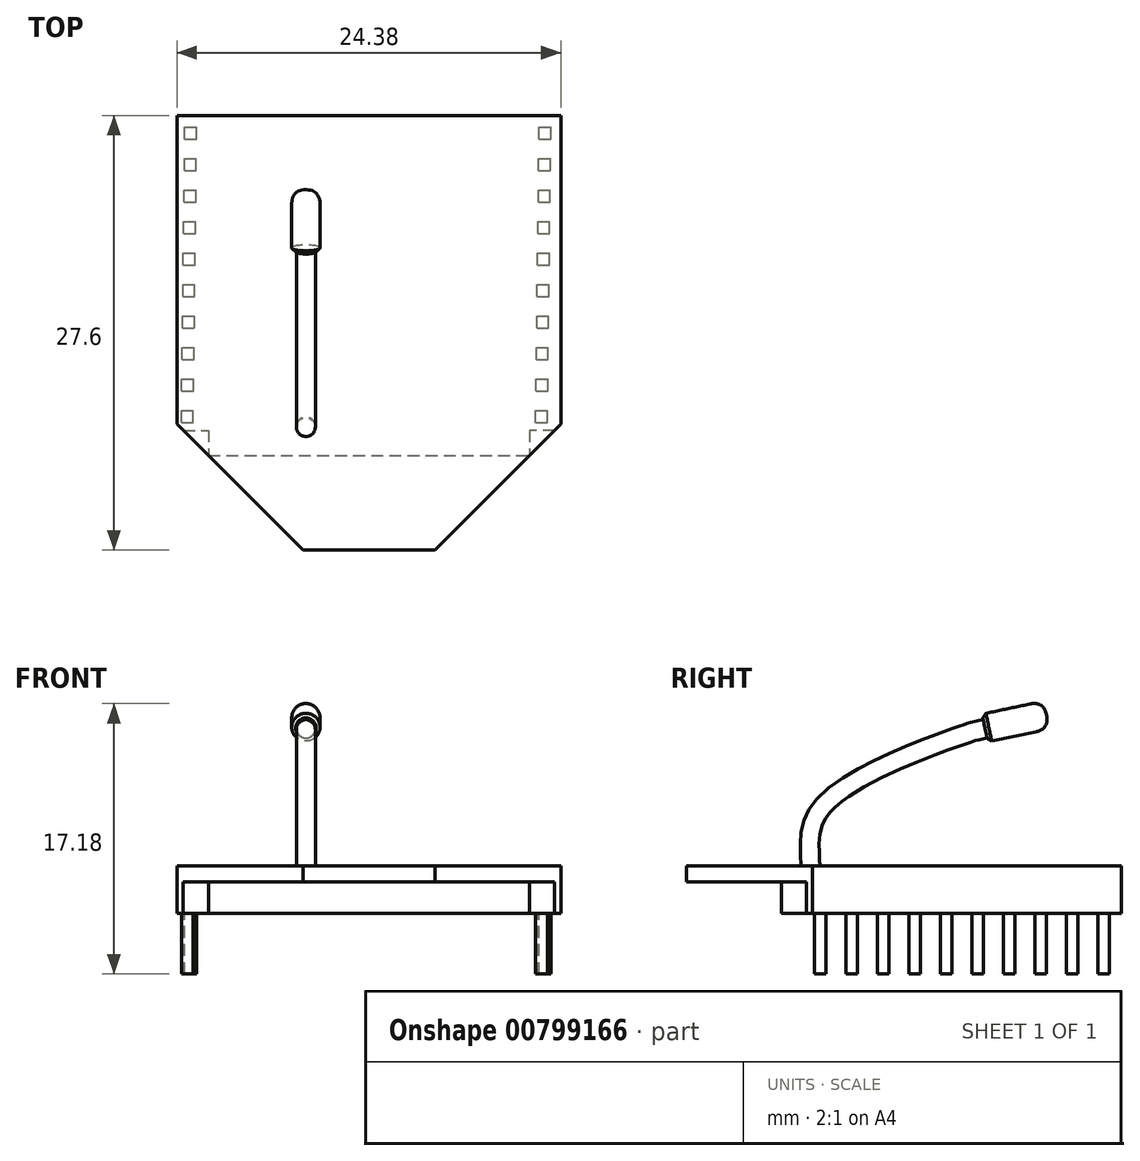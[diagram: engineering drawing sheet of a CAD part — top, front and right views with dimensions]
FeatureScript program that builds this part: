
annotation { "Feature Type Name" : "Feature", "Feature Type Description" : "" }
export const myFeature = defineFeature(function(context is Context, id is Id, definition is map)
    precondition{}
    {
        {
            var Q0;
            Q0=qCreatedBy(makeId("Top.planeOp"),FACE);
            var sketch = newSketch(context, id + "F0", { "sketchPlane" : qUnion([Q0])});
            skLineSegment(sketch, "E0.bottom", {"start": v(-12.19, 13.8) * mm, "end": v(12.2, 13.8) * mm});
            skLineSegment(sketch, "E0.top", {"start": v(-12.2, -13.8) * mm, "end": v(12.2, -13.8) * mm});
            skLineSegment(sketch, "E0.left", {"start": v(-12.19, 13.8) * mm, "end": v(-12.2, -13.8) * mm});
            skLineSegment(sketch, "E0.right", {"start": v(12.2, 13.8) * mm, "end": v(12.19, -13.8) * mm});
            skPoint(sketch, "E0.middle", {"position": v(0, 0) * mm});
            skSolve(sketch);
        }
        {
            var Q0;
            Q0 = qSketchRegion(id + "F0", true);
            extrude(context, id + "F1", {"entities" : qUnion([Q0]), "oppositeDirection" : true, "depth" : 1 * mm, "offsetDistance" : 25 * mm});
        }
        {
            var Q0;
            Q0=makeQuery(id+"F1.opExtrude","CAP_FACE",FACE,{"disambiguationData":[OSD([sQuery(id+"F0.wireOp",EDGE,"E0.bottom"),sQuery(id+"F0.wireOp",EDGE,"E0.top"),sQuery(id+"F0.wireOp",EDGE,"E0.left"),sQuery(id+"F0.wireOp",EDGE,"E0.right")])],"isStart":false});
            var sketch = newSketch(context, id + "F2", { "sketchPlane" : qUnion([Q0])});
            skLineSegment(sketch, "E1.bottom", {"start": v(-12.19, -13.8) * mm, "end": v(-10.19, -13.8) * mm});
            skLineSegment(sketch, "E1.top", {"start": v(-12.2, 6.2) * mm, "end": v(-10.2, 6.2) * mm});
            skLineSegment(sketch, "E1.left", {"start": v(-12.19, -13.8) * mm, "end": v(-12.19, 6.2) * mm});
            skLineSegment(sketch, "E1.right", {"start": v(-10.19, -13.8) * mm, "end": v(-10.2, 6.2) * mm});
            skLineSegment(sketch, "E2.bottom", {"start": v(12.2, -13.8) * mm, "end": v(10.2, -13.8) * mm});
            skLineSegment(sketch, "E2.top", {"start": v(12.2, 6.2) * mm, "end": v(10.2, 6.2) * mm});
            skLineSegment(sketch, "E2.left", {"start": v(12.2, -13.8) * mm, "end": v(12.2, 6.2) * mm});
            skLineSegment(sketch, "E2.right", {"start": v(10.2, -13.8) * mm, "end": v(10.2, 6.2) * mm});
            skSolve(sketch);
        }
        {
            var Q0;
            Q0=makeQuery(id+"F2.imprint","IMPRINT",FACE,{"disambiguationData":[TD([[makeQuery(id+"F2.imprint","IMPRINT",EDGE,{"derivedFrom":sQuery(id+"F2.wireOp",EDGE,"E1.bottom")}),1.0]])]});
            var Q1;
            Q1=makeQuery(id+"F2.imprint","IMPRINT",FACE,{"disambiguationData":[TD([[makeQuery(id+"F2.imprint","IMPRINT",EDGE,{"derivedFrom":sQuery(id+"F2.wireOp",EDGE,"E2.bottom")}),1.0]])]});
            extrude(context, id + "F3", {"entities" : qUnion([Q0, Q1]), "operationType" : NewBodyOperationType.ADD, "depth" : 2 * mm, "offsetDistance" : 25 * mm});
        }
        {
            var Q0;
            Q0=makeQuery(id+"F3.opExtrude","CAP_FACE",FACE,{"disambiguationData":[OSD([sQuery(id+"F2.wireOp",EDGE,"E1.bottom"),sQuery(id+"F2.wireOp",EDGE,"E1.top"),sQuery(id+"F2.wireOp",EDGE,"E1.left"),sQuery(id+"F2.wireOp",EDGE,"E1.right")])],"isStart":false});
            var sketch = newSketch(context, id + "F4", { "sketchPlane" : qUnion([Q0])});
            skLineSegment(sketch, "E3.bottom", {"start": v(-11.69, -12.3) * mm, "end": v(-10.94, -12.3) * mm});
            skLineSegment(sketch, "E3.top", {"start": v(-11.69, -13.05) * mm, "end": v(-10.94, -13.05) * mm});
            skLineSegment(sketch, "E3.left", {"start": v(-11.69, -12.3) * mm, "end": v(-11.69, -13.05) * mm});
            skLineSegment(sketch, "E3.right", {"start": v(-10.94, -12.3) * mm, "end": v(-10.94, -13.05) * mm});
            skLineSegment(sketch, "E4.0.1.0", {"start": v(-11.71, -10.3) * mm, "end": v(-10.96, -10.3) * mm});
            skLineSegment(sketch, "E4.0.1.1", {"start": v(-10.96, -10.3) * mm, "end": v(-10.96, -11.06) * mm});
            skLineSegment(sketch, "E4.0.1.2", {"start": v(-11.71, -10.3) * mm, "end": v(-11.71, -11.06) * mm});
            skLineSegment(sketch, "E4.0.1.3", {"start": v(-11.71, -11.06) * mm, "end": v(-10.96, -11.06) * mm});
            skLineSegment(sketch, "E4.0.2.0", {"start": v(-11.74, -8.3) * mm, "end": v(-10.99, -8.3) * mm});
            skLineSegment(sketch, "E4.0.2.1", {"start": v(-10.99, -8.3) * mm, "end": v(-10.99, -9.06) * mm});
            skLineSegment(sketch, "E4.0.2.2", {"start": v(-11.74, -8.3) * mm, "end": v(-11.74, -9.06) * mm});
            skLineSegment(sketch, "E4.0.2.3", {"start": v(-11.74, -9.06) * mm, "end": v(-10.99, -9.06) * mm});
            skLineSegment(sketch, "E4.0.3.0", {"start": v(-11.76, -6.3) * mm, "end": v(-11.01, -6.3) * mm});
            skLineSegment(sketch, "E4.0.3.1", {"start": v(-11.01, -6.3) * mm, "end": v(-11.01, -7.06) * mm});
            skLineSegment(sketch, "E4.0.3.2", {"start": v(-11.76, -6.3) * mm, "end": v(-11.76, -7.06) * mm});
            skLineSegment(sketch, "E4.0.3.3", {"start": v(-11.76, -7.06) * mm, "end": v(-11.01, -7.06) * mm});
            skLineSegment(sketch, "E4.0.4.0", {"start": v(-11.79, -4.3) * mm, "end": v(-11.04, -4.3) * mm});
            skLineSegment(sketch, "E4.0.4.1", {"start": v(-11.04, -4.3) * mm, "end": v(-11.04, -5.06) * mm});
            skLineSegment(sketch, "E4.0.4.2", {"start": v(-11.79, -4.3) * mm, "end": v(-11.79, -5.06) * mm});
            skLineSegment(sketch, "E4.0.4.3", {"start": v(-11.79, -5.06) * mm, "end": v(-11.04, -5.06) * mm});
            skLineSegment(sketch, "E4.0.5.0", {"start": v(-11.81, -2.3) * mm, "end": v(-11.06, -2.3) * mm});
            skLineSegment(sketch, "E4.0.5.1", {"start": v(-11.06, -2.3) * mm, "end": v(-11.06, -3.06) * mm});
            skLineSegment(sketch, "E4.0.5.2", {"start": v(-11.81, -2.3) * mm, "end": v(-11.81, -3.06) * mm});
            skLineSegment(sketch, "E4.0.5.3", {"start": v(-11.81, -3.06) * mm, "end": v(-11.06, -3.06) * mm});
            skLineSegment(sketch, "E4.0.6.0", {"start": v(-11.83, -0.3) * mm, "end": v(-11.08, -0.3) * mm});
            skLineSegment(sketch, "E4.0.6.1", {"start": v(-11.08, -0.3) * mm, "end": v(-11.08, -1.06) * mm});
            skLineSegment(sketch, "E4.0.6.2", {"start": v(-11.83, -0.3) * mm, "end": v(-11.83, -1.06) * mm});
            skLineSegment(sketch, "E4.0.6.3", {"start": v(-11.83, -1.06) * mm, "end": v(-11.08, -1.06) * mm});
            skLineSegment(sketch, "E4.0.7.0", {"start": v(-11.86, 1.7) * mm, "end": v(-11.1, 1.7) * mm});
            skLineSegment(sketch, "E4.0.7.1", {"start": v(-11.1, 1.7) * mm, "end": v(-11.1, 0.94) * mm});
            skLineSegment(sketch, "E4.0.7.2", {"start": v(-11.86, 1.7) * mm, "end": v(-11.86, 0.94) * mm});
            skLineSegment(sketch, "E4.0.7.3", {"start": v(-11.86, 0.94) * mm, "end": v(-11.1, 0.94) * mm});
            skLineSegment(sketch, "E4.0.8.0", {"start": v(-11.88, 3.7) * mm, "end": v(-11.13, 3.7) * mm});
            skLineSegment(sketch, "E4.0.8.1", {"start": v(-11.13, 3.7) * mm, "end": v(-11.13, 2.94) * mm});
            skLineSegment(sketch, "E4.0.8.2", {"start": v(-11.88, 3.7) * mm, "end": v(-11.88, 2.94) * mm});
            skLineSegment(sketch, "E4.0.8.3", {"start": v(-11.88, 2.94) * mm, "end": v(-11.13, 2.94) * mm});
            skLineSegment(sketch, "E4.0.9.0", {"start": v(-11.9, 5.7) * mm, "end": v(-11.16, 5.7) * mm});
            skLineSegment(sketch, "E4.0.9.1", {"start": v(-11.16, 5.7) * mm, "end": v(-11.16, 4.94) * mm});
            skLineSegment(sketch, "E4.0.9.2", {"start": v(-11.9, 5.7) * mm, "end": v(-11.9, 4.94) * mm});
            skLineSegment(sketch, "E4.0.9.3", {"start": v(-11.9, 4.94) * mm, "end": v(-11.16, 4.94) * mm});
            skLineSegment(sketch, "E4.1.0.0", {"start": v(10.81, -12.3) * mm, "end": v(11.56, -12.3) * mm});
            skLineSegment(sketch, "E4.1.0.1", {"start": v(11.56, -12.3) * mm, "end": v(11.56, -13.05) * mm});
            skLineSegment(sketch, "E4.1.0.2", {"start": v(10.81, -12.3) * mm, "end": v(10.81, -13.05) * mm});
            skLineSegment(sketch, "E4.1.0.3", {"start": v(10.81, -13.05) * mm, "end": v(11.56, -13.05) * mm});
            skLineSegment(sketch, "E4.1.1.0", {"start": v(10.79, -10.3) * mm, "end": v(11.54, -10.3) * mm});
            skLineSegment(sketch, "E4.1.1.1", {"start": v(11.54, -10.3) * mm, "end": v(11.54, -11.06) * mm});
            skLineSegment(sketch, "E4.1.1.2", {"start": v(10.79, -10.3) * mm, "end": v(10.79, -11.06) * mm});
            skLineSegment(sketch, "E4.1.1.3", {"start": v(10.79, -11.06) * mm, "end": v(11.54, -11.06) * mm});
            skLineSegment(sketch, "E4.1.2.0", {"start": v(10.76, -8.3) * mm, "end": v(11.51, -8.3) * mm});
            skLineSegment(sketch, "E4.1.2.1", {"start": v(11.51, -8.3) * mm, "end": v(11.51, -9.06) * mm});
            skLineSegment(sketch, "E4.1.2.2", {"start": v(10.76, -8.3) * mm, "end": v(10.76, -9.06) * mm});
            skLineSegment(sketch, "E4.1.2.3", {"start": v(10.76, -9.06) * mm, "end": v(11.51, -9.06) * mm});
            skLineSegment(sketch, "E4.1.3.0", {"start": v(10.74, -6.3) * mm, "end": v(11.49, -6.3) * mm});
            skLineSegment(sketch, "E4.1.3.1", {"start": v(11.49, -6.3) * mm, "end": v(11.49, -7.06) * mm});
            skLineSegment(sketch, "E4.1.3.2", {"start": v(10.74, -6.3) * mm, "end": v(10.74, -7.06) * mm});
            skLineSegment(sketch, "E4.1.3.3", {"start": v(10.74, -7.06) * mm, "end": v(11.49, -7.06) * mm});
            skLineSegment(sketch, "E4.1.4.0", {"start": v(10.71, -4.3) * mm, "end": v(11.46, -4.3) * mm});
            skLineSegment(sketch, "E4.1.4.1", {"start": v(11.46, -4.3) * mm, "end": v(11.46, -5.06) * mm});
            skLineSegment(sketch, "E4.1.4.2", {"start": v(10.71, -4.3) * mm, "end": v(10.71, -5.06) * mm});
            skLineSegment(sketch, "E4.1.4.3", {"start": v(10.71, -5.06) * mm, "end": v(11.46, -5.06) * mm});
            skLineSegment(sketch, "E4.1.5.0", {"start": v(10.69, -2.3) * mm, "end": v(11.44, -2.3) * mm});
            skLineSegment(sketch, "E4.1.5.1", {"start": v(11.44, -2.3) * mm, "end": v(11.44, -3.06) * mm});
            skLineSegment(sketch, "E4.1.5.2", {"start": v(10.69, -2.3) * mm, "end": v(10.69, -3.06) * mm});
            skLineSegment(sketch, "E4.1.5.3", {"start": v(10.69, -3.06) * mm, "end": v(11.44, -3.06) * mm});
            skLineSegment(sketch, "E4.1.6.0", {"start": v(10.67, -0.3) * mm, "end": v(11.42, -0.3) * mm});
            skLineSegment(sketch, "E4.1.6.1", {"start": v(11.42, -0.3) * mm, "end": v(11.42, -1.06) * mm});
            skLineSegment(sketch, "E4.1.6.2", {"start": v(10.67, -0.3) * mm, "end": v(10.67, -1.06) * mm});
            skLineSegment(sketch, "E4.1.6.3", {"start": v(10.67, -1.06) * mm, "end": v(11.42, -1.06) * mm});
            skLineSegment(sketch, "E4.1.7.0", {"start": v(10.64, 1.7) * mm, "end": v(11.4, 1.7) * mm});
            skLineSegment(sketch, "E4.1.7.1", {"start": v(11.4, 1.7) * mm, "end": v(11.4, 0.94) * mm});
            skLineSegment(sketch, "E4.1.7.2", {"start": v(10.64, 1.7) * mm, "end": v(10.64, 0.94) * mm});
            skLineSegment(sketch, "E4.1.7.3", {"start": v(10.64, 0.94) * mm, "end": v(11.4, 0.94) * mm});
            skLineSegment(sketch, "E4.1.8.0", {"start": v(10.62, 3.7) * mm, "end": v(11.37, 3.7) * mm});
            skLineSegment(sketch, "E4.1.8.1", {"start": v(11.37, 3.7) * mm, "end": v(11.37, 2.94) * mm});
            skLineSegment(sketch, "E4.1.8.2", {"start": v(10.62, 3.7) * mm, "end": v(10.62, 2.94) * mm});
            skLineSegment(sketch, "E4.1.8.3", {"start": v(10.62, 2.94) * mm, "end": v(11.37, 2.94) * mm});
            skLineSegment(sketch, "E4.1.9.0", {"start": v(10.6, 5.7) * mm, "end": v(11.34, 5.7) * mm});
            skLineSegment(sketch, "E4.1.9.1", {"start": v(11.34, 5.7) * mm, "end": v(11.34, 4.94) * mm});
            skLineSegment(sketch, "E4.1.9.2", {"start": v(10.6, 5.7) * mm, "end": v(10.6, 4.94) * mm});
            skLineSegment(sketch, "E4.1.9.3", {"start": v(10.6, 4.94) * mm, "end": v(11.34, 4.94) * mm});
            skLineSegment(sketch, "E4.direction1", {"start": v(-11.69, -13.05) * mm, "end": v(10.81, -13.05) * mm, "construction": true});
            skLineSegment(sketch, "E4.direction2", {"start": v(-11.69, -13.05) * mm, "end": v(-11.71, -11.06) * mm, "construction": true});
            skSolve(sketch);
        }
        {
            var Q0;
            Q0=makeQuery(id+"F4.imprint","IMPRINT",FACE,{"disambiguationData":[TD([[makeQuery(id+"F4.imprint","IMPRINT",EDGE,{"derivedFrom":sQuery(id+"F4.wireOp",EDGE,"E3.bottom")}),-1.0]])]});
            var Q1;
            Q1=makeQuery(id+"F4.imprint","IMPRINT",FACE,{"disambiguationData":[TD([[makeQuery(id+"F4.imprint","IMPRINT",EDGE,{"derivedFrom":sQuery(id+"F4.wireOp",EDGE,"E4.0.1.0")}),-1.0]])]});
            var Q2;
            Q2=makeQuery(id+"F4.imprint","IMPRINT",FACE,{"disambiguationData":[TD([[makeQuery(id+"F4.imprint","IMPRINT",EDGE,{"derivedFrom":sQuery(id+"F4.wireOp",EDGE,"E4.0.2.0")}),-1.0]])]});
            var Q3;
            Q3=makeQuery(id+"F4.imprint","IMPRINT",FACE,{"disambiguationData":[TD([[makeQuery(id+"F4.imprint","IMPRINT",EDGE,{"derivedFrom":sQuery(id+"F4.wireOp",EDGE,"E4.0.3.0")}),-1.0]])]});
            var Q4;
            Q4=makeQuery(id+"F4.imprint","IMPRINT",FACE,{"disambiguationData":[TD([[makeQuery(id+"F4.imprint","IMPRINT",EDGE,{"derivedFrom":sQuery(id+"F4.wireOp",EDGE,"E4.0.4.0")}),-1.0]])]});
            var Q5;
            Q5=makeQuery(id+"F4.imprint","IMPRINT",FACE,{"disambiguationData":[TD([[makeQuery(id+"F4.imprint","IMPRINT",EDGE,{"derivedFrom":sQuery(id+"F4.wireOp",EDGE,"E4.0.5.0")}),-1.0]])]});
            var Q6;
            Q6=makeQuery(id+"F4.imprint","IMPRINT",FACE,{"disambiguationData":[TD([[makeQuery(id+"F4.imprint","IMPRINT",EDGE,{"derivedFrom":sQuery(id+"F4.wireOp",EDGE,"E4.0.6.0")}),-1.0]])]});
            var Q7;
            Q7=makeQuery(id+"F4.imprint","IMPRINT",FACE,{"disambiguationData":[TD([[makeQuery(id+"F4.imprint","IMPRINT",EDGE,{"derivedFrom":sQuery(id+"F4.wireOp",EDGE,"E4.0.7.0")}),-1.0]])]});
            var Q8;
            Q8=makeQuery(id+"F4.imprint","IMPRINT",FACE,{"disambiguationData":[TD([[makeQuery(id+"F4.imprint","IMPRINT",EDGE,{"derivedFrom":sQuery(id+"F4.wireOp",EDGE,"E4.0.8.0")}),-1.0]])]});
            var Q9;
            Q9=makeQuery(id+"F4.imprint","IMPRINT",FACE,{"disambiguationData":[TD([[makeQuery(id+"F4.imprint","IMPRINT",EDGE,{"derivedFrom":sQuery(id+"F4.wireOp",EDGE,"E4.0.9.0")}),-1.0]])]});
            var Q10;
            Q10=makeQuery(id+"F4.imprint","IMPRINT",FACE,{"disambiguationData":[TD([[makeQuery(id+"F4.imprint","IMPRINT",EDGE,{"derivedFrom":sQuery(id+"F4.wireOp",EDGE,"E4.1.9.0")}),-1.0]])]});
            var Q11;
            Q11=makeQuery(id+"F4.imprint","IMPRINT",FACE,{"disambiguationData":[TD([[makeQuery(id+"F4.imprint","IMPRINT",EDGE,{"derivedFrom":sQuery(id+"F4.wireOp",EDGE,"E4.1.8.0")}),-1.0]])]});
            var Q12;
            Q12=makeQuery(id+"F4.imprint","IMPRINT",FACE,{"disambiguationData":[TD([[makeQuery(id+"F4.imprint","IMPRINT",EDGE,{"derivedFrom":sQuery(id+"F4.wireOp",EDGE,"E4.1.7.0")}),-1.0]])]});
            var Q13;
            Q13=makeQuery(id+"F4.imprint","IMPRINT",FACE,{"disambiguationData":[TD([[makeQuery(id+"F4.imprint","IMPRINT",EDGE,{"derivedFrom":sQuery(id+"F4.wireOp",EDGE,"E4.1.6.0")}),-1.0]])]});
            var Q14;
            Q14=makeQuery(id+"F4.imprint","IMPRINT",FACE,{"disambiguationData":[TD([[makeQuery(id+"F4.imprint","IMPRINT",EDGE,{"derivedFrom":sQuery(id+"F4.wireOp",EDGE,"E4.1.5.0")}),-1.0]])]});
            var Q15;
            Q15=makeQuery(id+"F4.imprint","IMPRINT",FACE,{"disambiguationData":[TD([[makeQuery(id+"F4.imprint","IMPRINT",EDGE,{"derivedFrom":sQuery(id+"F4.wireOp",EDGE,"E4.1.4.0")}),-1.0]])]});
            var Q16;
            Q16=makeQuery(id+"F4.imprint","IMPRINT",FACE,{"disambiguationData":[TD([[makeQuery(id+"F4.imprint","IMPRINT",EDGE,{"derivedFrom":sQuery(id+"F4.wireOp",EDGE,"E4.1.3.0")}),-1.0]])]});
            var Q17;
            Q17=makeQuery(id+"F4.imprint","IMPRINT",FACE,{"disambiguationData":[TD([[makeQuery(id+"F4.imprint","IMPRINT",EDGE,{"derivedFrom":sQuery(id+"F4.wireOp",EDGE,"E4.1.2.0")}),-1.0]])]});
            var Q18;
            Q18=makeQuery(id+"F4.imprint","IMPRINT",FACE,{"disambiguationData":[TD([[makeQuery(id+"F4.imprint","IMPRINT",EDGE,{"derivedFrom":sQuery(id+"F4.wireOp",EDGE,"E4.1.1.0")}),-1.0]])]});
            var Q19;
            Q19=makeQuery(id+"F4.imprint","IMPRINT",FACE,{"disambiguationData":[TD([[makeQuery(id+"F4.imprint","IMPRINT",EDGE,{"derivedFrom":sQuery(id+"F4.wireOp",EDGE,"E4.1.0.0")}),-1.0]])]});
            extrude(context, id + "F5", {"entities" : qUnion([Q0, Q1, Q2, Q3, Q4, Q5, Q6, Q7, Q8, Q9, Q10, Q11, Q12, Q13, Q14, Q15, Q16, Q17, Q18, Q19]), "operationType" : NewBodyOperationType.ADD, "depth" : (6.86 - (1 + 2)) * mm, "offsetDistance" : 25 * mm});
        }
        {
            var Q0;
            Q0=makeQuery(id+"F1.opExtrude","SWEPT_EDGE",EDGE,{"disambiguationData":[OSD([sQuery(id+"F0.wireOp",EDGE,"E0.top"),sQuery(id+"F0.wireOp",EDGE,"E0.right")])]});
            var Q1;
            Q1=makeQuery(id+"F1.opExtrude","SWEPT_EDGE",EDGE,{"disambiguationData":[OSD([sQuery(id+"F0.wireOp",EDGE,"E0.top"),sQuery(id+"F0.wireOp",EDGE,"E0.left")])]});
            chamfer(context, id + "F6", {"entities" : qUnion([Q0, Q1]), "width" : 8 * mm, "tangentPropagation" : true});
        }
        {
            var Q0;
            Q0=makeQuery(id+"F1.opExtrude","CAP_FACE",FACE,{"disambiguationData":[OSD([sQuery(id+"F0.wireOp",EDGE,"E0.bottom"),sQuery(id+"F0.wireOp",EDGE,"E0.top"),sQuery(id+"F0.wireOp",EDGE,"E0.left"),sQuery(id+"F0.wireOp",EDGE,"E0.right")])],"isStart":false});
            var sketch = newSketch(context, id + "F7", { "sketchPlane" : qUnion([Q0])});
            skLineSegment(sketch, "E5.bottom", {"start": v(-10.19, -13.8) * mm, "end": v(10.2, -13.8) * mm});
            skLineSegment(sketch, "E5.top", {"start": v(-10.19, 7.8) * mm, "end": v(10.2, 7.8) * mm});
            skLineSegment(sketch, "E5.left", {"start": v(-10.2, -13.8) * mm, "end": v(-10.2, 7.8) * mm});
            skLineSegment(sketch, "E5.right", {"start": v(10.2, -13.8) * mm, "end": v(10.2, 7.8) * mm});
            skSolve(sketch);
        }
        {
            var Q0;
            {var subQ2=sQuery(id+"F7.wireOp",EDGE,"E5.top");Q0=makeQuery(id+"F7.imprint","IMPRINT",FACE,{"disambiguationData":[TD([[makeQuery(id+"F7.imprint","IMPRINT",EDGE,{"derivedFrom":subQ2}),-1.0]])]});}
            extrude(context, id + "F8", {"entities" : qUnion([Q0]), "operationType" : NewBodyOperationType.ADD, "depth" : 2 * mm, "offsetDistance" : 25 * mm});
        }
        {
            var Q0;
            Q0=qCreatedBy(makeId("Right.planeOp"),FACE);
            cPlane(context, id + "F9", {"entities" : qUnion([Q0]), "cplaneType" : CPlaneType.OFFSET, "offset" : 4 * mm, "oppositeDirection" : true, "width" : 150 * mm, "height" : 150 * mm});
        }
        {
            var Q0;
            Q0=qCreatedBy(id+"F9.planeOp",FACE);
            var sketch = newSketch(context, id + "F10", { "sketchPlane" : qUnion([Q0])});
            skFitSpline(sketch, "E6", {"points": [v(-5.95, 0) * mm, v(-4.96, 4) * mm, v(3.85, 8.37) * mm, v(9.06, 9.6) * mm], "startDerivative": vector(-0.35, 15.25) * mm, "endDerivative": vector(50.53, 11.9) * mm});
            skSolve(sketch);
        }
        {
            var Q0;
            Q0=makeQuery(id+"F1.opExtrude","CAP_FACE",FACE,{"disambiguationData":[OSD([sQuery(id+"F0.wireOp",EDGE,"E0.bottom"),sQuery(id+"F0.wireOp",EDGE,"E0.top"),sQuery(id+"F0.wireOp",EDGE,"E0.left"),sQuery(id+"F0.wireOp",EDGE,"E0.right")])],"isStart":true});
            var sketch = newSketch(context, id + "F11", { "sketchPlane" : qUnion([Q0])});
            skCircle(sketch, "E7", {"center": v(-4, -5.95) * mm, "radius": 0.6 * mm});
            skSolve(sketch);
        }
        {
            var Q0;
            Q0=makeQuery(id+"F11.imprint","IMPRINT",FACE,{"disambiguationData":[TD([[makeQuery(id+"F11.imprint","IMPRINT",EDGE,{"derivedFrom":sQuery(id+"F11.wireOp",EDGE,"E7")}),1.0]])]});
            var Q1;
            Q1=sQuery(id+"F10.wireOp",EDGE,"E6");
            sweep(context, id + "F12", {"operationType" : NewBodyOperationType.ADD, "profiles" : qUnion([Q0]), "path" : qUnion([Q1])});
        }
        {
            var Q0;
            Q0=makeQuery(id+"F12.opSweep","CAP_FACE",FACE,{"disambiguationData":[OSD([sQuery(id+"F10.wireOp",VERTEX,"E6.end"),sQuery(id+"F11.wireOp",EDGE,"E7")])],"isStart":false});
            var sketch = newSketch(context, id + "F13", { "sketchPlane" : qUnion([Q0])});
            skCircle(sketch, "E8", {"center": v(4, 7.51) * mm, "radius": 0.9 * mm});
            skSolve(sketch);
        }
        {
            var Q0;
            Q0=makeQuery(id+"F13.imprint","IMPRINT",FACE,{"disambiguationData":[TD([[makeQuery(id+"F13.imprint","IMPRINT",EDGE,{"derivedFrom":sQuery(id+"F13.wireOp",EDGE,"E8")}),1.0]])]});
            var Q1;
            Q1=makeQuery(id+"F13.imprint","IMPRINT",FACE,{"disambiguationData":[TD([[makeQuery(id+"F13.imprint","IMPRINT",EDGE,{"derivedFrom":makeQuery(id+"F12.opSweep","CAP_EDGE",EDGE,{"disambiguationData":[OSD([sQuery(id+"F10.wireOp",VERTEX,"E6.end"),sQuery(id+"F11.wireOp",EDGE,"E7")])],"isStart":false})}),1.0]])]});
            extrude(context, id + "F14", {"entities" : qUnion([Q0, Q1]), "operationType" : NewBodyOperationType.ADD, "oppositeDirection" : true, "depth" : 4 * mm, "offsetDistance" : 25 * mm});
        }
        {
            var Q0;
            Q0=makeQuery(id+"F14.opExtrude","CAP_EDGE",EDGE,{"disambiguationData":[OSD([sQuery(id+"F13.wireOp",EDGE,"E8")])],"isStart":true});
            fillet(context, id + "F15", {"entities" : qUnion([Q0]), "radius" : 0.9 * mm, "rho" : 0.5, "crossSection" : FilletCrossSection.CONIC, "allowEdgeOverflow" : false});
        }
        {
            var Q0;
            Q0=makeQuery(id+"F14.opExtrude","CAP_EDGE",EDGE,{"disambiguationData":[OSD([sQuery(id+"F13.wireOp",EDGE,"E8")])],"isStart":false});
            chamfer(context, id + "F16", {"entities" : qUnion([Q0]), "width" : .25 * mm, "tangentPropagation" : true});
        }
    });
